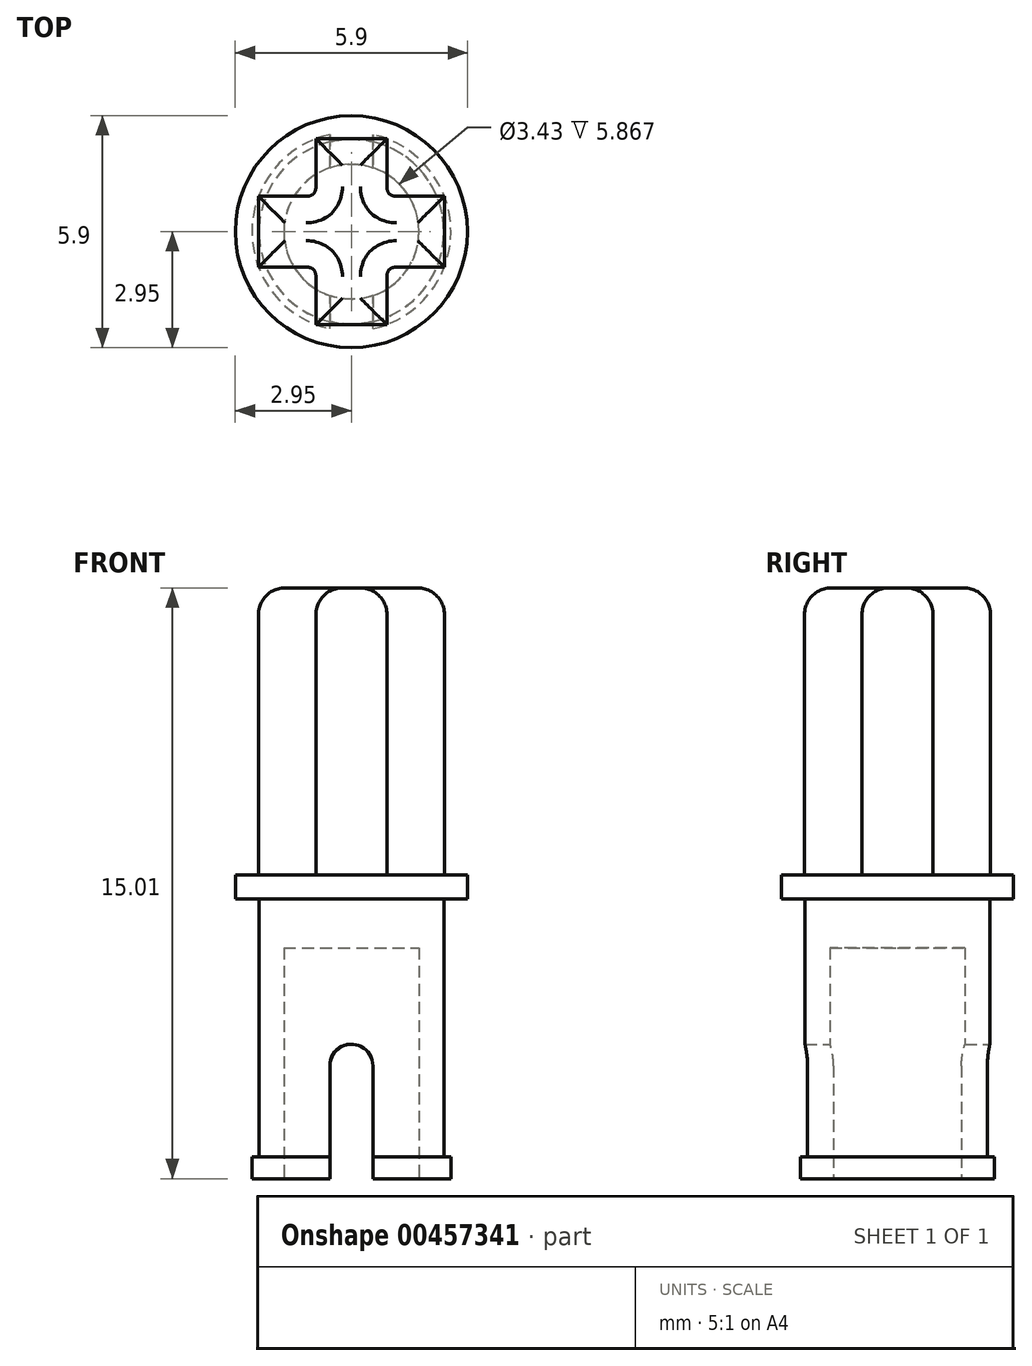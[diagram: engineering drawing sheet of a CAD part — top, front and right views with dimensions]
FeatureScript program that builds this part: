
annotation { "Feature Type Name" : "Feature", "Feature Type Description" : "" }
export const myFeature = defineFeature(function(context is Context, id is Id, definition is map)
    precondition{}
    {
        {
            var Q0;
            Q0=qCreatedBy(makeId("Top.planeOp"),FACE);
            var sketch = newSketch(context, id + "F0", { "sketchPlane" : qUnion([Q0])});
            skCircle(sketch, "E0", {"center": v(0, 0) * mm, "radius": 2.35 * mm});
            skSolve(sketch);
        }
        {
            var Q0;
            Q0=qSketchRegion(id+"F0",true);
            extrude(context, id + "F1", {"entities" : qUnion([Q0]), "depth" : 15.67 * mm});
        }
        {
            var Q0;
            Q0=qCreatedBy(makeId("Front.planeOp"),FACE);
            var sketch = newSketch(context, id + "F2", { "sketchPlane" : qUnion([Q0])});
            skLineSegment(sketch, "E1.bottom", {"start": v(0.55, -2.87) * mm, "end": v(-0.55, -2.87) * mm});
            skLineSegment(sketch, "E1.top", {"start": v(0.55, 2.87) * mm, "end": v(-0.55, 2.87) * mm});
            skLineSegment(sketch, "E1.left", {"start": v(0.55, -2.87) * mm, "end": v(0.55, 2.87) * mm});
            skLineSegment(sketch, "E1.right", {"start": v(-0.55, -2.87) * mm, "end": v(-0.55, 2.87) * mm});
            skPoint(sketch, "E1.middle", {"position": v(0, 0) * mm});
            skCircle(sketch, "E2", {"center": v(0, 2.87) * mm, "radius": 0.55 * mm});
            skSolve(sketch);
        }
        {
            var Q0;
            Q0=makeQuery(id+"F1.opExtrude","CAP_FACE",FACE,{"disambiguationData":[OSD([sQuery(id+"F0.wireOp",EDGE,"E0")])],"isStart":true});
            var sketch = newSketch(context, id + "F3", { "sketchPlane" : qUnion([Q0])});
            skCircle(sketch, "E3", {"center": v(0, 0) * mm, "radius": 2.53 * mm});
            skSolve(sketch);
        }
        {
            var Q0;
            Q0=qSketchRegion(id+"F3",true);
            extrude(context, id + "F4", {"entities" : qUnion([Q0]), "operationType" : NewBodyOperationType.ADD, "oppositeDirection" : true, "depth" : 0.56 * mm});
        }
        {
            var Q0;
            Q0=qSketchRegion(id+"F2",true);
            extrude(context, id + "F5", {"entities" : qUnion([Q0]), "operationType" : NewBodyOperationType.REMOVE, "depth" : 25.4 * mm, "symmetric" : true});
        }
        {
            var Q0;
            Q0=makeQuery(id+"F1.opExtrude","CAP_FACE",FACE,{"disambiguationData":[OSD([sQuery(id+"F0.wireOp",EDGE,"E0")])],"isStart":false});
            var sketch = newSketch(context, id + "F6", { "sketchPlane" : qUnion([Q0])});
            skCircle(sketch, "E4", {"center": v(0, 0) * mm, "radius": 2.95 * mm});
            skSolve(sketch);
        }
        {
            var Q0;
            Q0=qSketchRegion(id+"F6",true);
            extrude(context, id + "F7", {"entities" : qUnion([Q0]), "operationType" : NewBodyOperationType.ADD, "oppositeDirection" : true, "depth" : 8.56 * mm});
        }
        {
            var Q0;
            Q0=makeQuery(id+"F7.boolean.opBoolean","MERGE",FACE,{"derivedFrom":[makeQuery(id+"F1.opExtrude","CAP_FACE",FACE,{"disambiguationData":[OSD([sQuery(id+"F0.wireOp",EDGE,"E0")])],"isStart":false}),makeQuery(id+"F7.opExtrude","CAP_FACE",FACE,{"disambiguationData":[OSD([sQuery(id+"F6.wireOp",EDGE,"E4")])],"isStart":true})]});
            var sketch = newSketch(context, id + "F8", { "sketchPlane" : qUnion([Q0])});
            skCircle(sketch, "E5", {"center": v(0, 0) * mm, "radius": 12.7 * mm});
            skSolve(sketch);
        }
        {
            var Q0;
            Q0=qSketchRegion(id+"F8",true);
            extrude(context, id + "F9", {"entities" : qUnion([Q0]), "operationType" : NewBodyOperationType.REMOVE, "oppositeDirection" : true, "depth" : 7.95 * mm});
        }
        {
            var Q0;
            Q0=makeQuery(id+"F9.boolean.opBoolean","COPY",FACE,{"derivedFrom":makeQuery(id+"F9.opExtrude","CAP_FACE",FACE,{"disambiguationData":[OSD([sQuery(id+"F8.wireOp",EDGE,"E5")])],"isStart":false})});
            var sketch = newSketch(context, id + "F10", { "sketchPlane" : qUnion([Q0])});
            skLineSegment(sketch, "E6.bottom", {"start": v(2.36, -0.9) * mm, "end": v(-2.36, -0.9) * mm});
            skLineSegment(sketch, "E6.top", {"start": v(2.36, 0.9) * mm, "end": v(-2.36, 0.9) * mm});
            skLineSegment(sketch, "E6.left", {"start": v(2.36, -0.9) * mm, "end": v(2.36, 0.9) * mm});
            skLineSegment(sketch, "E6.right", {"start": v(-2.36, -0.9) * mm, "end": v(-2.36, 0.9) * mm});
            skPoint(sketch, "E6.middle", {"position": v(0, 0) * mm});
            skLineSegment(sketch, "E7.bottom", {"start": v(-0.9, -2.36) * mm, "end": v(0.9, -2.36) * mm});
            skLineSegment(sketch, "E7.top", {"start": v(-0.9, 2.36) * mm, "end": v(0.9, 2.36) * mm});
            skLineSegment(sketch, "E7.left", {"start": v(-0.9, -2.36) * mm, "end": v(-0.9, 2.36) * mm});
            skLineSegment(sketch, "E7.right", {"start": v(0.9, -2.36) * mm, "end": v(0.9, 2.36) * mm});
            skSolve(sketch);
        }
        {
            var Q0;
            Q0=qSketchRegion(id+"F10",true);
            extrude(context, id + "F11", {"entities" : qUnion([Q0]), "operationType" : NewBodyOperationType.ADD, "depth" : 7.3 * mm});
        }
        {
            var Q0;
            Q0=makeQuery(id+"F11.opExtrude","SWEPT_EDGE",EDGE,{"disambiguationData":[OSD([sQuery(id+"F10.wireOp",EDGE,"E6.bottom"),sQuery(id+"F10.wireOp",EDGE,"E7.left")])]});
            var Q1;
            Q1=makeQuery(id+"F11.opExtrude","SWEPT_EDGE",EDGE,{"disambiguationData":[OSD([sQuery(id+"F10.wireOp",EDGE,"E6.top"),sQuery(id+"F10.wireOp",EDGE,"E7.right")])]});
            var Q2;
            Q2=makeQuery(id+"F11.opExtrude","SWEPT_EDGE",EDGE,{"disambiguationData":[OSD([sQuery(id+"F10.wireOp",EDGE,"E6.bottom"),sQuery(id+"F10.wireOp",EDGE,"E7.right")])]});
            var Q3;
            Q3=makeQuery(id+"F11.opExtrude","SWEPT_EDGE",EDGE,{"disambiguationData":[OSD([sQuery(id+"F10.wireOp",EDGE,"E6.top"),sQuery(id+"F10.wireOp",EDGE,"E7.left")])]});
            fillet(context, id + "F12", {"entities" : qUnion([Q0, Q1, Q2, Q3]), "radius" : 0.25 * mm, "tangentPropagation" : true, "rho" : 0.5, "crossSection" : FilletCrossSection.CONIC, "allowEdgeOverflow" : false});
        }
        {
            var Q0;
            Q0=makeQuery(id+"F11.opExtrude","CAP_FACE",FACE,{"disambiguationData":[OSD([sQuery(id+"F10.wireOp",EDGE,"E6.bottom"),sQuery(id+"F10.wireOp",EDGE,"E6.top"),sQuery(id+"F10.wireOp",EDGE,"E6.left"),sQuery(id+"F10.wireOp",EDGE,"E6.right"),sQuery(id+"F10.wireOp",EDGE,"E7.bottom"),sQuery(id+"F10.wireOp",EDGE,"E7.top"),sQuery(id+"F10.wireOp",EDGE,"E7.left"),sQuery(id+"F10.wireOp",EDGE,"E7.right")])],"isStart":false});
            fillet(context, id + "F13", {"entities" : qUnion([Q0]), "radius" : 0.67 * mm, "tangentPropagation" : true, "allowEdgeOverflow" : false});
        }
        {
            var Q0;
            {var subQ0=sQuery(id+"F3.wireOp",EDGE,"E3");Q0=makeQuery(id+"F5.boolean.opBoolean","SPLIT",FACE,{"disambiguationData":[TD([makeQuery(id+"F5.opExtrude","SWEPT_FACE",FACE,{"disambiguationData":[OSD([sQuery(id+"F2.wireOp",EDGE,"E1.left")])]})])],"derivedFrom":makeQuery(id+"F4.boolean.opBoolean","MERGE",FACE,{"derivedFrom":[makeQuery(id+"F1.opExtrude","CAP_FACE",FACE,{"disambiguationData":[OSD([sQuery(id+"F0.wireOp",EDGE,"E0")])],"isStart":true}),makeQuery(id+"F4.opExtrude","CAP_FACE",FACE,{"disambiguationData":[OSD([subQ0])],"isStart":true})]})});}
            var sketch = newSketch(context, id + "F14", { "sketchPlane" : qUnion([Q0])});
            skCircle(sketch, "E8", {"center": v(0, 0) * mm, "radius": 1.71 * mm});
            skSolve(sketch);
        }
        {
            var Q0;
            Q0=qSketchRegion(id+"F14",true);
            extrude(context, id + "F15", {"entities" : qUnion([Q0]), "operationType" : NewBodyOperationType.REMOVE, "oppositeDirection" : true, "depth" : 5.87 * mm});
        }
    });
